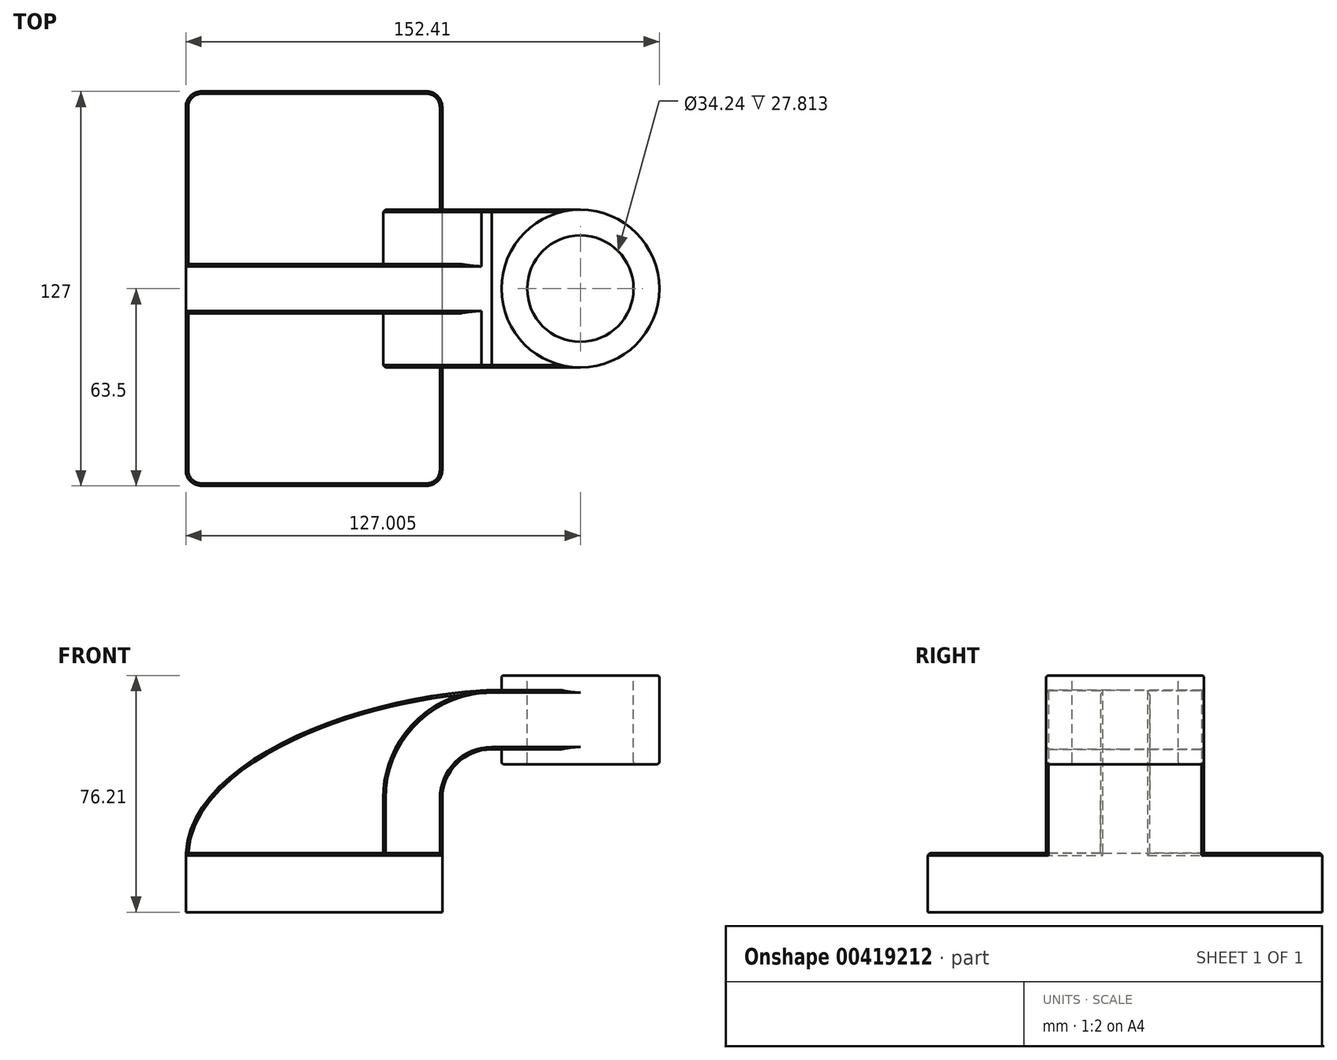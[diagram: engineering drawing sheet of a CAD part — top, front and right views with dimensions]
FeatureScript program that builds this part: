
annotation { "Feature Type Name" : "Feature", "Feature Type Description" : "" }
export const myFeature = defineFeature(function(context is Context, id is Id, definition is map)
    precondition{}
    {
        {
            var Q0;
            Q0=qCreatedBy(makeId("Front.planeOp"),FACE);
            var sketch = newSketch(context, id + "F0", { "sketchPlane" : qUnion([Q0])});
            skLineSegment(sketch, "E0.rect.bottom", {"start": v(-41.28, 9.52) * mm, "end": v(41.28, 9.52) * mm});
            skLineSegment(sketch, "E0.rect.top", {"start": v(-41.28, -9.52) * mm, "end": v(41.28, -9.52) * mm});
            skLineSegment(sketch, "E0.rect.left", {"start": v(-41.28, 9.52) * mm, "end": v(-41.28, -9.52) * mm});
            skLineSegment(sketch, "E0.rect.right", {"start": v(41.28, 9.52) * mm, "end": v(41.28, -9.52) * mm});
            skPoint(sketch, "E0.rect.middle", {"position": v(0, 0) * mm});
            skLineSegment(sketch, "E1", {"start": v(41.28, 9.52) * mm, "end": v(41.28, 27) * mm});
            skArc(sketch, "E2", {"start": v(41.28, 27) * mm, "mid": v(45.92, 38.23) * mm, "end": v(57.15, 42.88) * mm});
            skLineSegment(sketch, "E3", {"start": v(57.15, 42.88) * mm, "end": v(85.72, 42.88) * mm});
            skLineSegment(sketch, "E4.rect.bottom", {"start": v(60.32, 38.1) * mm, "end": v(111.12, 38.1) * mm});
            skLineSegment(sketch, "E4.rect.top", {"start": v(60.32, 66.68) * mm, "end": v(111.12, 66.68) * mm});
            skLineSegment(sketch, "E4.rect.left", {"start": v(60.32, 38.1) * mm, "end": v(60.32, 66.68) * mm});
            skLineSegment(sketch, "E4.rect.right", {"start": v(111.13, 38.1) * mm, "end": v(111.12, 66.68) * mm});
            skPoint(sketch, "E4.rect.middle", {"position": v(85.72, 52.39) * mm});
            skLineSegment(sketch, "E5.0", {"start": v(57.15, 61.93) * mm, "end": v(85.72, 61.93) * mm});
            skArc(sketch, "E5.1", {"start": v(22.23, 27) * mm, "mid": v(32.45, 51.7) * mm, "end": v(57.15, 61.93) * mm});
            skLineSegment(sketch, "E5.2", {"start": v(22.23, 9.52) * mm, "end": v(22.23, 27) * mm});
            skLineSegment(sketch, "E6", {"start": v(85.72, 38.1) * mm, "end": v(85.72, 66.68) * mm});
            skFitSpline(sketch, "E7", {"points": [v(-41.28, 9.53) * mm, v(57.15, 61.93) * mm], "startDerivative": vector(5.2, 92.34) * mm, "endDerivative": vector(120.92, 4.22) * mm});
            skSolve(sketch);
        }
        {
            var Q0;
            Q0=makeQuery(id+"F0.imprint","IMPRINT",FACE,{"disambiguationData":[TD([[makeQuery(id+"F0.imprint","IMPRINT",EDGE,{"derivedFrom":sQuery(id+"F0.wireOp",EDGE,"E0.rect.top")}),1.0]])]});
            extrude(context, id + "F1", {"entities" : qUnion([Q0]), "endBound" : BoundingType.SYMMETRIC, "depth" : 127 * mm});
        }
        {
            var Q0;
            {var subQ9=sQuery(id+"F0.wireOp",EDGE,"E1");Q0=makeQuery(id+"F0.imprint","IMPRINT",FACE,{"disambiguationData":[TD([[makeQuery(id+"F0.imprint","IMPRINT",EDGE,{"derivedFrom":subQ9}),1.0]])]});}
            var Q1;
            {var subQ0=sQuery(id+"F0.wireOp",EDGE,"E6");var subQ1=sQuery(id+"F0.wireOp",EDGE,"E3");var subQ2=makeQuery(id+"F0.imprint","INTERSECT",VERTEX,{"derivedFrom":[subQ1,subQ0]});Q1=makeQuery(id+"F0.imprint","IMPRINT",FACE,{"disambiguationData":[TD([[makeQuery(id+"F0.imprint","IMPRINT",EDGE,{"disambiguationData":[TD([[subQ2,1.0]])],"derivedFrom":subQ1}),1.0]])]});}
            extrude(context, id + "F2", {"entities" : qUnion([Q0, Q1]), "operationType" : NewBodyOperationType.ADD, "endBound" : BoundingType.SYMMETRIC, "depth" : 50.8 * mm});
        }
        {
            var Q0;
            {var subQ3=sQuery(id+"F0.wireOp",EDGE,"E5.2");Q0=makeQuery(id+"F0.imprint","IMPRINT",FACE,{"disambiguationData":[TD([[makeQuery(id+"F0.imprint","IMPRINT",EDGE,{"derivedFrom":subQ3}),1.0]])]});}
            extrude(context, id + "F3", {"entities" : qUnion([Q0]), "operationType" : NewBodyOperationType.ADD, "endBound" : BoundingType.SYMMETRIC, "depth" : 15.88 * mm});
        }
        {
            var Q0;
            {var subQ5=sQuery(id+"F0.wireOp",EDGE,"E4.rect.right");Q0=makeQuery(id+"F0.imprint","IMPRINT",FACE,{"disambiguationData":[TD([[makeQuery(id+"F0.imprint","IMPRINT",EDGE,{"derivedFrom":subQ5}),1.0]])]});}
            var Q1;
            Q1=sQuery(id+"F0.wireOp",EDGE,"E6");
            revolve(context, id + "F4", {"operationType" : NewBodyOperationType.ADD, "entities" : qUnion([Q0]), "axis" : qUnion([Q1]), "revolveType" : RevolveType.FULL});
        }
        {
            var Q0;
            Q0=makeQuery(id+"F1.opExtrude","CAP_EDGE",EDGE,{"disambiguationData":[OSD([sQuery(id+"F0.wireOp",EDGE,"E0.rect.right")])],"isStart":false});
            var Q1;
            Q1=makeQuery(id+"F1.opExtrude","CAP_EDGE",EDGE,{"disambiguationData":[OSD([sQuery(id+"F0.wireOp",EDGE,"E0.rect.left")])],"isStart":false});
            var Q2;
            Q2=makeQuery(id+"F1.opExtrude","CAP_EDGE",EDGE,{"disambiguationData":[OSD([sQuery(id+"F0.wireOp",EDGE,"E0.rect.right")])],"isStart":true});
            var Q3;
            Q3=makeQuery(id+"F1.opExtrude","CAP_EDGE",EDGE,{"disambiguationData":[OSD([sQuery(id+"F0.wireOp",EDGE,"E0.rect.left")])],"isStart":true});
            fillet(context, id + "F5", {"entities" : qUnion([Q0, Q1, Q2, Q3]), "radius" : 5.08 * mm, "tangentPropagation" : true, "allowEdgeOverflow" : false});
        }
        {
            var Q0;
            Q0=makeQuery(id+"F4.opRevolve","SWEPT_FACE",FACE,{"disambiguationData":[OSD([sQuery(id+"F0.wireOp",EDGE,"E4.rect.top")])]});
            var sketch = newSketch(context, id + "F6", { "sketchPlane" : qUnion([Q0])});
            skCircle(sketch, "E8", {"center": v(85.72, 0) * mm, "radius": 17.12 * mm});
            skSolve(sketch);
        }
        {
            var Q0;
            Q0=makeQuery(id+"F6.imprint","IMPRINT",FACE,{"disambiguationData":[TD([[makeQuery(id+"F6.imprint","IMPRINT",EDGE,{"derivedFrom":sQuery(id+"F6.wireOp",EDGE,"E8")}),1.0]])]});
            extrude(context, id + "F7", {"entities" : qUnion([Q0]), "operationType" : NewBodyOperationType.REMOVE, "endBound" : BoundingType.THROUGH_ALL, "oppositeDirection" : true, "depth" : 25.4 * mm});
        }
        {
            var Q0;
            Q0=makeQuery(id+"F7.boolean.opBoolean","INTERSECT",EDGE,{"derivedFrom":[makeQuery(id+"F4.opRevolve","SWEPT_FACE",FACE,{"disambiguationData":[OSD([sQuery(id+"F0.wireOp",EDGE,"E4.rect.bottom")])]}),makeQuery(id+"F7.opExtrude","SWEPT_FACE",FACE,{"disambiguationData":[OSD([sQuery(id+"F6.wireOp",EDGE,"E8")])]})]});
            var Q1;
            Q1=makeQuery(id+"F4.opRevolve","SWEPT_EDGE",EDGE,{"disambiguationData":[OSD([sQuery(id+"F0.wireOp",EDGE,"E4.rect.bottom"),sQuery(id+"F0.wireOp",EDGE,"E4.rect.right")])]});
            var Q2;
            Q2=makeQuery(id+"F7.boolean.opBoolean","COPY",EDGE,{"derivedFrom":makeQuery(id+"F7.opExtrude","CAP_EDGE",EDGE,{"disambiguationData":[OSD([sQuery(id+"F6.wireOp",EDGE,"E8")])],"isStart":true})});
            var Q3;
            Q3=makeQuery(id+"F4.opRevolve","SWEPT_EDGE",EDGE,{"disambiguationData":[OSD([sQuery(id+"F0.wireOp",EDGE,"E4.rect.top"),sQuery(id+"F0.wireOp",EDGE,"E4.rect.right")])]});
            fillet(context, id + "F8", {"entities" : qUnion([Q0, Q1, Q2, Q3]), "radius" : 0.76 * mm, "tangentPropagation" : true, "allowEdgeOverflow" : false});
        }
        {
            var Q0;
            Q0=makeQuery(id+"F3.opExtrude","CAP_EDGE",EDGE,{"disambiguationData":[OSD([sQuery(id+"F0.wireOp",EDGE,"E7")])],"isStart":true});
            var Q1;
            Q1=makeQuery(id+"F3.opExtrude","CAP_EDGE",EDGE,{"disambiguationData":[OSD([sQuery(id+"F0.wireOp",EDGE,"E7")])],"isStart":false});
            var Q2;
            Q2=makeQuery(id+"F2.opExtrude","CAP_EDGE",EDGE,{"disambiguationData":[OSD([sQuery(id+"F0.wireOp",EDGE,"E5.0")])],"isStart":true});
            var Q3;
            Q3=makeQuery(id+"F2.opExtrude","CAP_EDGE",EDGE,{"disambiguationData":[OSD([sQuery(id+"F0.wireOp",EDGE,"E7")])],"isStart":true});
            var Q4;
            Q4=makeQuery(id+"F2.opExtrude","CAP_EDGE",EDGE,{"disambiguationData":[OSD([sQuery(id+"F0.wireOp",EDGE,"E5.1")])],"isStart":true});
            var Q5;
            Q5=makeQuery(id+"F2.opExtrude","CAP_EDGE",EDGE,{"disambiguationData":[OSD([sQuery(id+"F0.wireOp",EDGE,"E5.2")])],"isStart":true});
            var Q6;
            Q6=makeQuery(id+"F2.opExtrude","CAP_EDGE",EDGE,{"disambiguationData":[OSD([sQuery(id+"F0.wireOp",EDGE,"E1")])],"isStart":true});
            var Q7;
            Q7=makeQuery(id+"F2.opExtrude","CAP_EDGE",EDGE,{"disambiguationData":[OSD([sQuery(id+"F0.wireOp",EDGE,"E2")])],"isStart":true});
            var Q8;
            Q8=makeQuery(id+"F2.opExtrude","CAP_EDGE",EDGE,{"disambiguationData":[OSD([sQuery(id+"F0.wireOp",EDGE,"E3")])],"isStart":true});
            var Q9;
            Q9=makeQuery(id+"F2.opExtrude","CAP_EDGE",EDGE,{"disambiguationData":[OSD([sQuery(id+"F0.wireOp",EDGE,"E5.0")])],"isStart":false});
            var Q10;
            Q10=makeQuery(id+"F2.opExtrude","CAP_EDGE",EDGE,{"disambiguationData":[OSD([sQuery(id+"F0.wireOp",EDGE,"E7")])],"isStart":false});
            var Q11;
            Q11=makeQuery(id+"F2.opExtrude","CAP_EDGE",EDGE,{"disambiguationData":[OSD([sQuery(id+"F0.wireOp",EDGE,"E5.1")])],"isStart":false});
            var Q12;
            Q12=makeQuery(id+"F2.opExtrude","CAP_EDGE",EDGE,{"disambiguationData":[OSD([sQuery(id+"F0.wireOp",EDGE,"E5.2")])],"isStart":false});
            var Q13;
            Q13=makeQuery(id+"F2.opExtrude","CAP_EDGE",EDGE,{"disambiguationData":[OSD([sQuery(id+"F0.wireOp",EDGE,"E1")])],"isStart":false});
            var Q14;
            Q14=makeQuery(id+"F2.opExtrude","CAP_EDGE",EDGE,{"disambiguationData":[OSD([sQuery(id+"F0.wireOp",EDGE,"E2")])],"isStart":false});
            var Q15;
            Q15=makeQuery(id+"F2.opExtrude","CAP_EDGE",EDGE,{"disambiguationData":[OSD([sQuery(id+"F0.wireOp",EDGE,"E3")])],"isStart":false});
            chamfer(context, id + "F9", {"entities" : qUnion([Q0, Q1, Q2, Q3, Q4, Q5, Q6, Q7, Q8, Q9, Q10, Q11, Q12, Q13, Q14, Q15]), "width" : 0.76 * mm, "tangentPropagation" : true});
        }
        {
            var Q0;
            {var subQ0=sQuery(id+"F0.wireOp",EDGE,"E0.rect.left");var subQ1=sQuery(id+"F0.wireOp",EDGE,"E7");var subQ2=sQuery(id+"F0.wireOp",EDGE,"E0.rect.bottom");var subQ3=makeQuery(id+"F1.opExtrude","SWEPT_EDGE",EDGE,{"disambiguationData":[OSD([subQ2,subQ0,subQ1])]});Q0=makeQuery(id+"F9.opChamfer","MERGE",EDGE,{"derivedFrom":[makeQuery(id+"F3.boolean.opBoolean","MERGE",EDGE,{"derivedFrom":[subQ3,makeQuery(id+"F3.opExtrude","SWEPT_EDGE",EDGE,{"disambiguationData":[OSD([subQ2,subQ0,subQ1])]})]}),makeQuery(id+"F3.boolean.opBoolean","SPLIT",EDGE,{"disambiguationData":[TD([makeQuery(id+"F1.opExtrude","CAP_FACE",FACE,{"disambiguationData":[OSD([subQ2,sQuery(id+"F0.wireOp",EDGE,"E0.rect.top"),subQ0,sQuery(id+"F0.wireOp",EDGE,"E0.rect.right")])],"isStart":true})])],"derivedFrom":subQ3})]});}
            var Q1;
            {var subQ0=sQuery(id+"F0.wireOp",EDGE,"E1");var subQ1=sQuery(id+"F0.wireOp",EDGE,"E0.rect.bottom");var subQ2=sQuery(id+"F0.wireOp",EDGE,"E0.rect.right");Q1=makeQuery(id+"F2.boolean.opBoolean","SPLIT",EDGE,{"disambiguationData":[TD([makeQuery(id+"F1.opExtrude","CAP_FACE",FACE,{"disambiguationData":[OSD([subQ1,sQuery(id+"F0.wireOp",EDGE,"E0.rect.top"),sQuery(id+"F0.wireOp",EDGE,"E0.rect.left"),subQ2])],"isStart":true})])],"derivedFrom":makeQuery(id+"F1.opExtrude","SWEPT_EDGE",EDGE,{"disambiguationData":[OSD([subQ1,subQ2,subQ0])]})});}
            var Q2;
            {var subQ4=sQuery(id+"F0.wireOp",EDGE,"E0.rect.bottom");var subQ5=sQuery(id+"F0.wireOp",EDGE,"E0.rect.right");var subQ6=sQuery(id+"F0.wireOp",EDGE,"E0.rect.left");Q2=makeQuery(id+"F5.opFillet","BLEND_EDGE",EDGE,{"blendedFrom":[makeQuery(id+"F1.opExtrude","CAP_EDGE",EDGE,{"disambiguationData":[OSD([subQ5])],"isStart":true}),makeQuery(id+"F3.boolean.opBoolean","SPLIT",FACE,{"disambiguationData":[TD([makeQuery(id+"F1.opExtrude","CAP_FACE",FACE,{"disambiguationData":[OSD([subQ4,sQuery(id+"F0.wireOp",EDGE,"E0.rect.top"),subQ6,subQ5])],"isStart":true})])],"derivedFrom":makeQuery(id+"F1.opExtrude","SWEPT_FACE",FACE,{"disambiguationData":[OSD([subQ4])]})})],"blendedInto":[makeQuery(id+"F3.boolean.opBoolean","SPLIT",FACE,{"disambiguationData":[TD([makeQuery(id+"F1.opExtrude","CAP_FACE",FACE,{"disambiguationData":[OSD([subQ4,sQuery(id+"F0.wireOp",EDGE,"E0.rect.top"),subQ6,subQ5])],"isStart":true})])],"derivedFrom":makeQuery(id+"F1.opExtrude","SWEPT_FACE",FACE,{"disambiguationData":[OSD([subQ4])]})})]});}
            var Q3;
            Q3=makeQuery(id+"F1.opExtrude","CAP_EDGE",EDGE,{"disambiguationData":[OSD([sQuery(id+"F0.wireOp",EDGE,"E0.rect.bottom")])],"isStart":true});
            var Q4;
            {var subQ4=sQuery(id+"F0.wireOp",EDGE,"E0.rect.bottom");var subQ5=sQuery(id+"F0.wireOp",EDGE,"E0.rect.right");var subQ6=sQuery(id+"F0.wireOp",EDGE,"E0.rect.left");Q4=makeQuery(id+"F5.opFillet","BLEND_EDGE",EDGE,{"blendedFrom":[makeQuery(id+"F1.opExtrude","CAP_EDGE",EDGE,{"disambiguationData":[OSD([subQ6])],"isStart":true}),makeQuery(id+"F3.boolean.opBoolean","SPLIT",FACE,{"disambiguationData":[TD([makeQuery(id+"F1.opExtrude","CAP_FACE",FACE,{"disambiguationData":[OSD([subQ4,sQuery(id+"F0.wireOp",EDGE,"E0.rect.top"),subQ6,subQ5])],"isStart":true})])],"derivedFrom":makeQuery(id+"F1.opExtrude","SWEPT_FACE",FACE,{"disambiguationData":[OSD([subQ4])]})})],"blendedInto":[makeQuery(id+"F3.boolean.opBoolean","SPLIT",FACE,{"disambiguationData":[TD([makeQuery(id+"F1.opExtrude","CAP_FACE",FACE,{"disambiguationData":[OSD([subQ4,sQuery(id+"F0.wireOp",EDGE,"E0.rect.top"),subQ6,subQ5])],"isStart":true})])],"derivedFrom":makeQuery(id+"F1.opExtrude","SWEPT_FACE",FACE,{"disambiguationData":[OSD([subQ4])]})})]});}
            var Q5;
            {var subQ4=sQuery(id+"F0.wireOp",EDGE,"E0.rect.bottom");var subQ5=sQuery(id+"F0.wireOp",EDGE,"E0.rect.right");var subQ6=sQuery(id+"F0.wireOp",EDGE,"E0.rect.left");Q5=makeQuery(id+"F5.opFillet","BLEND_EDGE",EDGE,{"blendedFrom":[makeQuery(id+"F1.opExtrude","CAP_EDGE",EDGE,{"disambiguationData":[OSD([subQ6])],"isStart":false}),makeQuery(id+"F3.boolean.opBoolean","SPLIT",FACE,{"disambiguationData":[TD([makeQuery(id+"F1.opExtrude","CAP_FACE",FACE,{"disambiguationData":[OSD([subQ4,sQuery(id+"F0.wireOp",EDGE,"E0.rect.top"),subQ6,subQ5])],"isStart":false})])],"derivedFrom":makeQuery(id+"F1.opExtrude","SWEPT_FACE",FACE,{"disambiguationData":[OSD([subQ4])]})})],"blendedInto":[makeQuery(id+"F3.boolean.opBoolean","SPLIT",FACE,{"disambiguationData":[TD([makeQuery(id+"F1.opExtrude","CAP_FACE",FACE,{"disambiguationData":[OSD([subQ4,sQuery(id+"F0.wireOp",EDGE,"E0.rect.top"),subQ6,subQ5])],"isStart":false})])],"derivedFrom":makeQuery(id+"F1.opExtrude","SWEPT_FACE",FACE,{"disambiguationData":[OSD([subQ4])]})})]});}
            var Q6;
            Q6=makeQuery(id+"F1.opExtrude","CAP_EDGE",EDGE,{"disambiguationData":[OSD([sQuery(id+"F0.wireOp",EDGE,"E0.rect.bottom")])],"isStart":false});
            var Q7;
            {var subQ4=sQuery(id+"F0.wireOp",EDGE,"E0.rect.bottom");var subQ5=sQuery(id+"F0.wireOp",EDGE,"E0.rect.right");var subQ6=sQuery(id+"F0.wireOp",EDGE,"E0.rect.left");Q7=makeQuery(id+"F5.opFillet","BLEND_EDGE",EDGE,{"blendedFrom":[makeQuery(id+"F1.opExtrude","CAP_EDGE",EDGE,{"disambiguationData":[OSD([subQ5])],"isStart":false}),makeQuery(id+"F3.boolean.opBoolean","SPLIT",FACE,{"disambiguationData":[TD([makeQuery(id+"F1.opExtrude","CAP_FACE",FACE,{"disambiguationData":[OSD([subQ4,sQuery(id+"F0.wireOp",EDGE,"E0.rect.top"),subQ6,subQ5])],"isStart":false})])],"derivedFrom":makeQuery(id+"F1.opExtrude","SWEPT_FACE",FACE,{"disambiguationData":[OSD([subQ4])]})})],"blendedInto":[makeQuery(id+"F3.boolean.opBoolean","SPLIT",FACE,{"disambiguationData":[TD([makeQuery(id+"F1.opExtrude","CAP_FACE",FACE,{"disambiguationData":[OSD([subQ4,sQuery(id+"F0.wireOp",EDGE,"E0.rect.top"),subQ6,subQ5])],"isStart":false})])],"derivedFrom":makeQuery(id+"F1.opExtrude","SWEPT_FACE",FACE,{"disambiguationData":[OSD([subQ4])]})})]});}
            var Q8;
            {var subQ0=sQuery(id+"F0.wireOp",EDGE,"E1");var subQ1=sQuery(id+"F0.wireOp",EDGE,"E0.rect.bottom");var subQ2=sQuery(id+"F0.wireOp",EDGE,"E0.rect.right");Q8=makeQuery(id+"F2.boolean.opBoolean","SPLIT",EDGE,{"disambiguationData":[TD([makeQuery(id+"F1.opExtrude","CAP_FACE",FACE,{"disambiguationData":[OSD([subQ1,sQuery(id+"F0.wireOp",EDGE,"E0.rect.top"),sQuery(id+"F0.wireOp",EDGE,"E0.rect.left"),subQ2])],"isStart":false})])],"derivedFrom":makeQuery(id+"F1.opExtrude","SWEPT_EDGE",EDGE,{"disambiguationData":[OSD([subQ1,subQ2,subQ0])]})});}
            var Q9;
            {var subQ0=sQuery(id+"F0.wireOp",EDGE,"E7");var subQ1=sQuery(id+"F0.wireOp",EDGE,"E0.rect.bottom");var subQ2=sQuery(id+"F0.wireOp",EDGE,"E0.rect.left");var subQ3=makeQuery(id+"F1.opExtrude","SWEPT_EDGE",EDGE,{"disambiguationData":[OSD([subQ1,subQ2,subQ0])]});Q9=makeQuery(id+"F9.opChamfer","MERGE",EDGE,{"derivedFrom":[makeQuery(id+"F3.boolean.opBoolean","MERGE",EDGE,{"derivedFrom":[subQ3,makeQuery(id+"F3.opExtrude","SWEPT_EDGE",EDGE,{"disambiguationData":[OSD([subQ1,subQ2,subQ0])]})]}),makeQuery(id+"F3.boolean.opBoolean","SPLIT",EDGE,{"disambiguationData":[TD([makeQuery(id+"F1.opExtrude","CAP_FACE",FACE,{"disambiguationData":[OSD([subQ1,sQuery(id+"F0.wireOp",EDGE,"E0.rect.top"),subQ2,sQuery(id+"F0.wireOp",EDGE,"E0.rect.right")])],"isStart":false})])],"derivedFrom":subQ3})]});}
            chamfer(context, id + "F10", {"entities" : qUnion([Q0, Q1, Q2, Q3, Q4, Q5, Q6, Q7, Q8, Q9]), "width" : 0.76 * mm, "tangentPropagation" : true});
        }
    });
